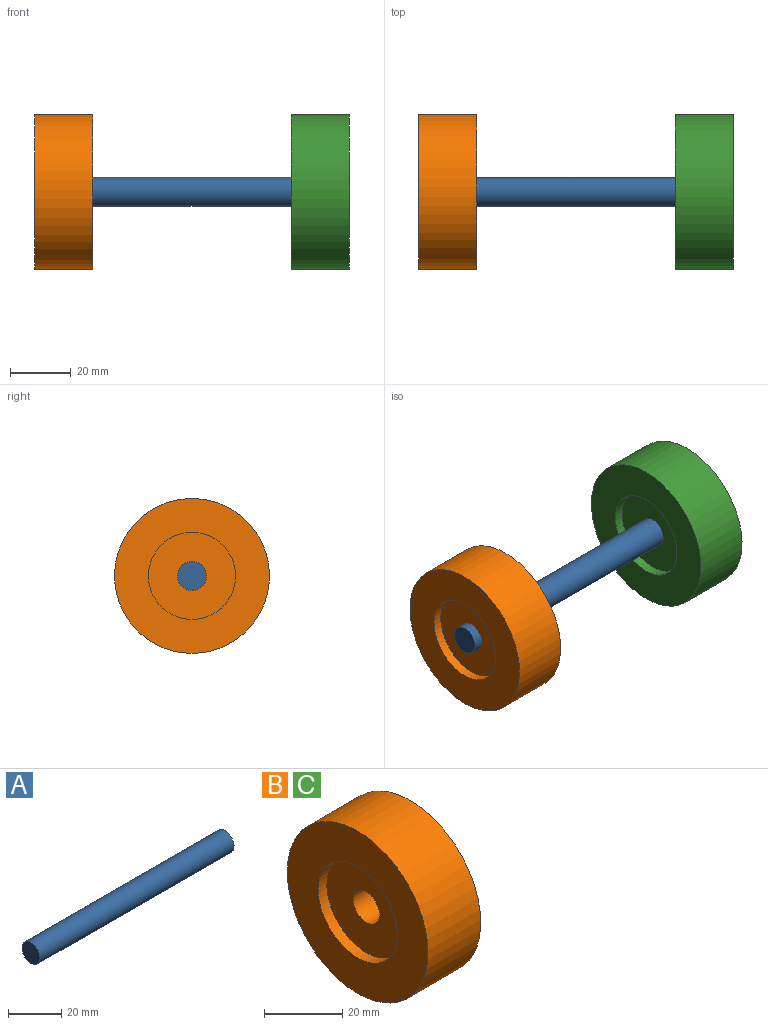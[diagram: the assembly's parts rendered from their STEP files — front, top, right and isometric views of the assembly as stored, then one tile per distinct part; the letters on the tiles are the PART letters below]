
ASSEMBLY  parts=3 mates=2
PART A: 3 faces, bbox 103.2x9.5x9.5 mm
  f0: cylinder r=4.76mm len=103.19mm, axis (-1,0,0), area 3087.7mm2, adj f1,f2
  f1: plane 9.53x9.53mm, normal (1,0,0), area 71.3mm2, adj f0
  f2: plane 9.53x9.53mm, normal (-1,0,0), area 71.3mm2, adj f0
PART B: 8 faces, bbox 19.1x50.8x50.8 mm
  f0: cylinder r=4.76mm len=12.7mm, axis (1,0,0), area 380mm2, adj f1,f7
  f1: plane 28.58x28.58mm, normal (-1,0,0), area 570mm2, adj f0,f2
  f2: cylinder r=14.29mm len=28.58mm, axis (1,0,0), area 285mm2, adj f1,f3
  f3: plane 50.8x50.8mm, normal (-1,0,0), area 1385.5mm2, adj f2,f4
  f4: cylinder r=25.4mm len=50.8mm, axis (1,0,0), area 3040.2mm2, adj f3,f5
  f5: plane 50.8x50.8mm, normal (1,0,0), area 1385.5mm2, adj f4,f6
  f6: cylinder r=14.29mm len=28.58mm, axis (1,0,0), area 285mm2, adj f5,f7
  f7: plane 28.58x28.58mm, normal (1,0,0), area 570mm2, adj f0,f6
PART C: same geometry as B
PLACE A t=(0,-41.28,-6.35)mm fixed
PLACE B t=(-84.14,-41.28,-6.35)mm
PLACE C t=(0,-41.28,-6.35)mm
MATE fastened C.f0 <-> A.f0  axis (1,0,0) through (51.59,0,0)mm
MATE fastened B.f0 <-> A.f0  axis (-1,0,0) through (-51.59,0,0)mm
